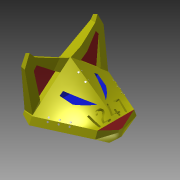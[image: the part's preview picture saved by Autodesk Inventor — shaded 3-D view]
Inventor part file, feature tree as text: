
AUTODESK INVENTOR PART (.ipt)
format: ipt  version: 2014 (Build 180170000, 170)  size: 811,520 bytes
history: native  units: in
note: dims shown in document units (in); Inventor stores cm internally (conversion verified against a paired STEP export)
features: sketch x18, extrude x11, plane x10, loft x4, projected_geometry x4, other x3, mirror x1, emboss x1
ambient origin geometry x8: Origin, YZ Plane, XZ Plane, XY Plane, X Axis, Y Axis, Z Axis, Center Point
bodies: Solid1 (feature_tree)
feature tree (52):
  sketch  "Sketch1"  dims[d0=0.7559in d1=0.7559in]
  plane  "Work Plane1"
  loft  "Loft1"
  extrude  "Extrusion1"  Depth=0.2in
  plane  "Work Plane4"
  loft  "Loft2"
  plane  "Work Plane5"
  loft  "Loft3"
  loft  "Loft4"
  extrude  "Extrusion2"  TaperAngle=0.0deg  [1 undecoded]
  plane  "Work Plane6"
  extrude  "Extrusion3"  Depth=1.0in
  extrude  "Extrusion4"  Depth=1.0651in
  extrude  "Extrusion5"  Depth=0.962in
  plane  "Work Plane7"
  extrude  "Extrusion6"  Depth=0.075in
  plane  "Work Plane8"
  other  "Work Axis1"
  plane  "Work Plane9"
  extrude  "Extrusion7"  Depth=0.06in
  mirror  "Mirror3"
  extrude  "Extrusion8"  Depth=0.05in
  plane  "Work Plane10"
  extrude  "Extrusion9"  Depth=0.0625in
  plane  "Work Plane11"
  extrude  "Extrusion10"  Depth=0.075in
  extrude  "Extrusion11"  TaperAngle=0.0deg  [1 undecoded]
  plane  "Work Plane12"
  emboss  "Emboss1"
  sketch  "Sketch2"  dims[d2=0.9963in d3=0.2in]
  sketch  "Sketch3"  dims[d4=0.5in d6=0.08in]
  sketch  "Sketch4"  dims[d7=0.55in d8=150.0deg]
  other  "Edges1"
  sketch  "Sketch5"  dims[d9=150.0deg d14=0.33in]
  projected_geometry  "Projected Loop1"
  other  "Edges2"
  sketch  "Sketch6"  dims[d15=0.66in d18=0.0in d19=90.0deg]
  sketch  "Sketch7"  dims[d20=0.0in d21=90.0deg d22=1.0in]
  sketch  "Sketch8"  dims[d26=1.0651in d28=1.0651in]
  sketch  "Sketch9"  dims[d29=0.0in d30=0.962in]
  sketch  "Sketch10"  dims[d31=0.962in d32=0.075in]
  sketch  "Sketch11"  dims[d33=0.15in d34=0.06in]
  sketch  "Sketch12"  dims[d35=0.1in d36=0.05in]
  sketch  "Sketch13"  dims[d37=0.45in d38=0.0in d39=0.0625in]
  projected_geometry  "Projected Loop2"
  projected_geometry  "Projected Loop3"
  sketch  "Sketch14"  dims[d40=0.01in d41=0.075in]
  projected_geometry  "Projected Loop4"
  sketch  "Sketch15"  dims[d42=0.01in d43=0.0in d44=90.0deg]
  sketch  "Sketch16"  dims[d45=0.0in d46=90.0deg]
  sketch  "Sketch17"  dims[d47=0.2in]
  sketch  "Sketch18"  dims[d48=0.07in d49=0.0in d50=90.0deg d51=0.0in d52=90.0deg d53=0.01in d54=0.01in d55=0.0344in d56=150.0deg d57=60.0deg d58=150.0deg d59=0.7in d60=0.05in d61=0.05in d62=0.05in d63=0.05in d64=0.05in d65=0.01in d66=0.0in d67=90.0deg d68=0.0in d69=90.0deg d70=0.1in d71=0.4in d72=0.15in d73=0.05in d74=0.0in d75=0.02in d77=0.15in d78=0.02in d79=0.1in d80=0.1in d81=0.1in d82=0.02in d83=0.15in d84=0.05in d85=0.0in d86=0.045in d87=0.0in d88=0.025in d89=0.0in d90=0.02in d91=0.02in d92=0.005in d93=0.0in d94=90.0deg d95=0.4466in d96=1.0in d97=0.0in d98=1.0in d99=0.0in d100=0.6528in d101=0.0in d102=0.0in d103=1.0in d104=0.0in d106=90.0deg d107=1.0in d108=0.0in d109=0.05in d110=0.0in]
note: 2 required parameter values undecoded (feature->parameter linkage not recoverable at this tier; creation-order binding heuristic only, values carry confidence <= 0.55)
